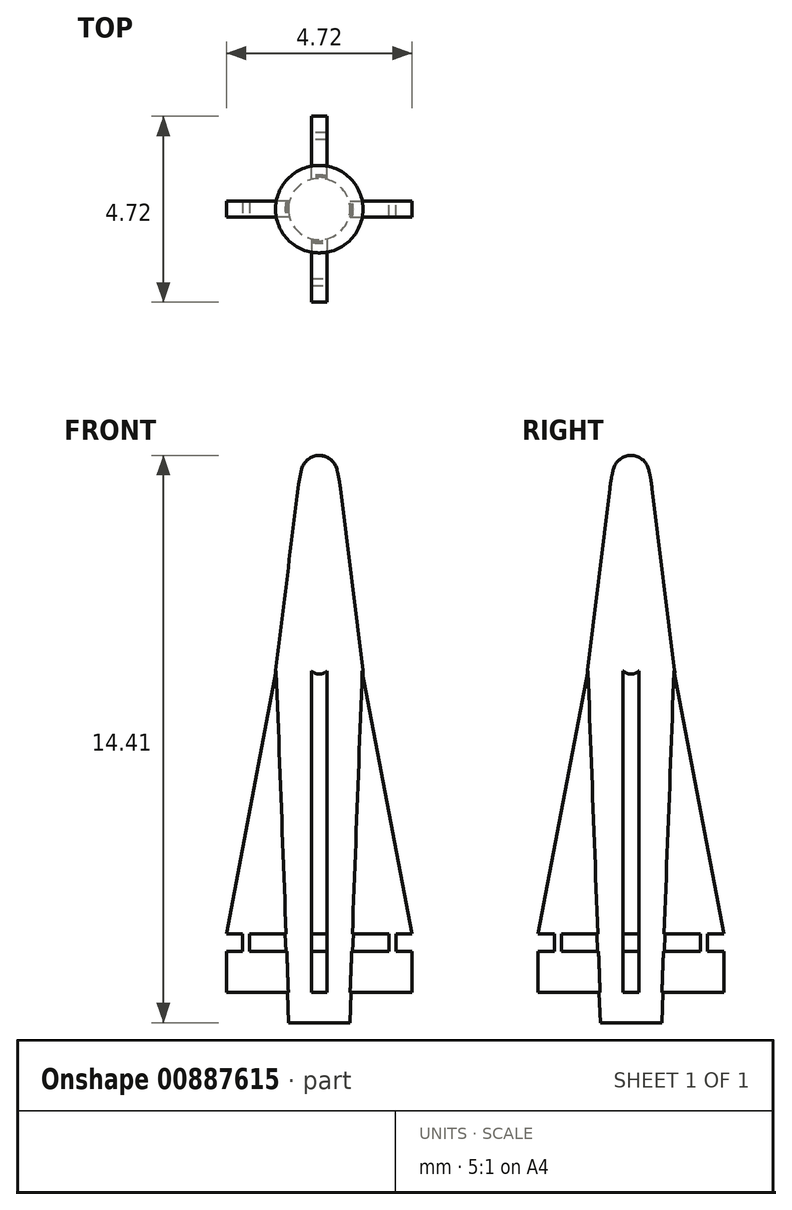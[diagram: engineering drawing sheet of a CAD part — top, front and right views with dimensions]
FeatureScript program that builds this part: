
annotation { "Feature Type Name" : "Feature", "Feature Type Description" : "" }
export const myFeature = defineFeature(function(context is Context, id is Id, definition is map)
    precondition{}
    {
        {
            var Q0;
            Q0=qCreatedBy(makeId("Front.planeOp"),FACE);
            var sketch = newSketch(context, id + "F0", { "sketchPlane" : qUnion([Q0])});
            skLineSegment(sketch, "E0", {"start": v(0, 0) * mm, "end": v(0, 14.4) * mm});
            skLineSegment(sketch, "E1", {"start": v(0.78, 0) * mm, "end": v(0, 0) * mm});
            skLineSegment(sketch, "E2", {"start": v(1.11, 8.92) * mm, "end": v(0.78, 0) * mm});
            skArc(sketch, "E3", {"start": v(0.45, 14.06) * mm, "mid": v(0.28, 14.31) * mm, "end": v(0, 14.4) * mm});
            skArc(sketch, "E4", {"start": v(0.54, 13.58) * mm, "mid": v(0.5, 13.82) * mm, "end": v(0.45, 14.06) * mm});
            skLineSegment(sketch, "E5", {"start": v(0.54, 13.58) * mm, "end": v(1.1, 8.95) * mm});
            skArc(sketch, "E6", {"start": v(1.11, 8.92) * mm, "mid": v(1.11, 8.93) * mm, "end": v(1.1, 8.95) * mm});
            skSolve(sketch);
        }
        {
            var Q0;
            {var subQ0=sQuery(id+"F0.wireOp",EDGE,"mrwio9nY-PsAZ-Zbfy-NhIU-sYq0QVbgGXAG");Q0=makeQuery(id+"F0.imprint","IMPRINT",FACE,{"disambiguationData":[TD([[makeQuery(id+"F0.imprint","IMPRINT",EDGE,{"derivedFrom":subQ0}),-1.0]])]});}
            var Q1;
            {var subQ7=sQuery(id+"F0.wireOp",EDGE,"E0");Q1=makeQuery(id+"F0.imprint","IMPRINT",FACE,{"disambiguationData":[TD([[makeQuery(id+"F0.imprint","IMPRINT",EDGE,{"derivedFrom":subQ7}),-1.0]])]});}
            var Q2;
            Q2=sQuery(id+"F0.wireOp",EDGE,"E0");
            revolve(context, id + "F1", {"surfaceOperationType" : NewSurfaceOperationType.NEW, "entities" : qUnion([Q0, Q1]), "axis" : qUnion([Q2]), "revolveType" : RevolveType.FULL});
        }
        {
            var Q0;
            Q0=qCreatedBy(makeId("Front.planeOp"),FACE);
            var sketch = newSketch(context, id + "F2", { "sketchPlane" : qUnion([Q0])});
            skLineSegment(sketch, "E7", {"start": v(0, 0) * mm, "end": v(0, 9.95) * mm});
            skLineSegment(sketch, "E8", {"start": v(0.4, 2.26) * mm, "end": v(0.4, 1.8) * mm});
            skLineSegment(sketch, "E9", {"start": v(0.4, 1.8) * mm, "end": v(2.36, 1.8) * mm});
            skLineSegment(sketch, "E10", {"start": v(0.4, 2.26) * mm, "end": v(2.36, 2.26) * mm});
            skLineSegment(sketch, "E11", {"start": v(2.36, 2.26) * mm, "end": v(0.9, 9.95) * mm});
            skPoint(sketch, "E12", {"position": v(-0.78, 2.26) * mm});
            skLineSegment(sketch, "E13", {"start": v(0, 0.76) * mm, "end": v(2.36, 0.76) * mm});
            skLineSegment(sketch, "E14", {"start": v(2.36, 0.76) * mm, "end": v(2.36, 1.8) * mm});
            skLineSegment(sketch, "E15", {"start": v(1.77, 2.26) * mm, "end": v(1.77, 1.8) * mm});
            skLineSegment(sketch, "E16", {"start": v(1.94, 2.26) * mm, "end": v(1.94, 1.8) * mm});
            skLineSegment(sketch, "E17.0", {"start": v(-0.78, 0) * mm, "end": v(0.78, 0) * mm});
            skLineSegment(sketch, "E18.0", {"start": v(1.11, 8.92) * mm, "end": v(-1.11, 8.92) * mm});
            skLineSegment(sketch, "E19", {"start": v(0.78, 0) * mm, "end": v(1.11, 8.92) * mm, "construction": true});
            skPoint(sketch, "E20", {"position": v(1.1, 8.85) * mm});
            skLineSegment(sketch, "E21", {"start": v(0.9, 9.95) * mm, "end": v(0, 9.95) * mm});
            skSolve(sketch);
        }
        {
            var Q0;
            Q0=qSketchRegion(id+"F2",true);
            extrude(context, id + "F3", {"entities" : qUnion([Q0]), "operationType" : NewBodyOperationType.ADD, "depth" : .4 * mm, "offsetDistance" : 25 * mm, "symmetric" : true});
        }
        {
            var Q0;
            Q0=makeQuery(id+"F1.opRevolve","SWEPT_BODY",BODY,{"disambiguationData":[OSD([sQuery(id+"F0.wireOp",EDGE,"E0"),sQuery(id+"F0.wireOp",EDGE,"55Lj6EjW-0Kk0-GJ5p-O6gq-hablAnl54JB5"),sQuery(id+"F0.wireOp",EDGE,"E1"),sQuery(id+"F0.wireOp",EDGE,"2EiOItwe-9FNA-eY8p-DkXH-AMy5AHyUmzZA"),sQuery(id+"F0.wireOp",EDGE,"lF35QjYl-MEgV-fRWE-0Yr6-Bt5vS8A7brRf")])]});
            var Q1;
            Q1=makeQuery(id+"F1.opRevolve","SWEPT_EDGE",EDGE,{"disambiguationData":[OSD([sQuery(id+"F0.wireOp",EDGE,"E4"),sQuery(id+"F0.wireOp",EDGE,"E5")])]});
            circularPattern(context, id + "F4", {"operationType" : NewBodyOperationType.ADD, "entities" : qUnion([Q0]), "axis" : qUnion([Q1]), "angle" : 360 * degree, "instanceCount" : 4, "equalSpace" : true, "computeTransformsWithoutBuiltin" : true});
        }
    });
